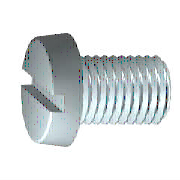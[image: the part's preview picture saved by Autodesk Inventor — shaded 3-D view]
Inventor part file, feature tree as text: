
AUTODESK INVENTOR PART (.ipt)
format: ipt  version: 2017 (Build 210142000, 142)  size: 187,904 bytes
history: native  units: mm (DEFAULTED — no unit token found)
features: sketch x2, extrude x1, plane x1
ambient origin geometry x7: Origin, YZ Plane, XZ Plane, X Axis, Y Axis, Z Axis, Center Point
bodies: Solid1 (feature_tree), Body (feature_tree)
feature tree (4):
  sketch  "Sketch2"  dims[d2=0.306825mm d3=2.0mm d4=3.0mm d5=2.729367mm d8=90.0deg d7=0.0mm d9=5.5mm d10=0.872665mm d11=0.8mm d12=5.5mm d14=0.1mm d15=3.0mm d16=0.0mm d17=0.270635mm d18=0.306825mm d19=0.85mm d20=0.0mm d36=45.0deg d37=0.0mm d39=0.0mm]
  extrude  "Slot"  Depth=3.0mm
  plane  "Work Plane1"
  sketch  "Sketch1"  dims[d0=4.0mm d1=3.0mm]
